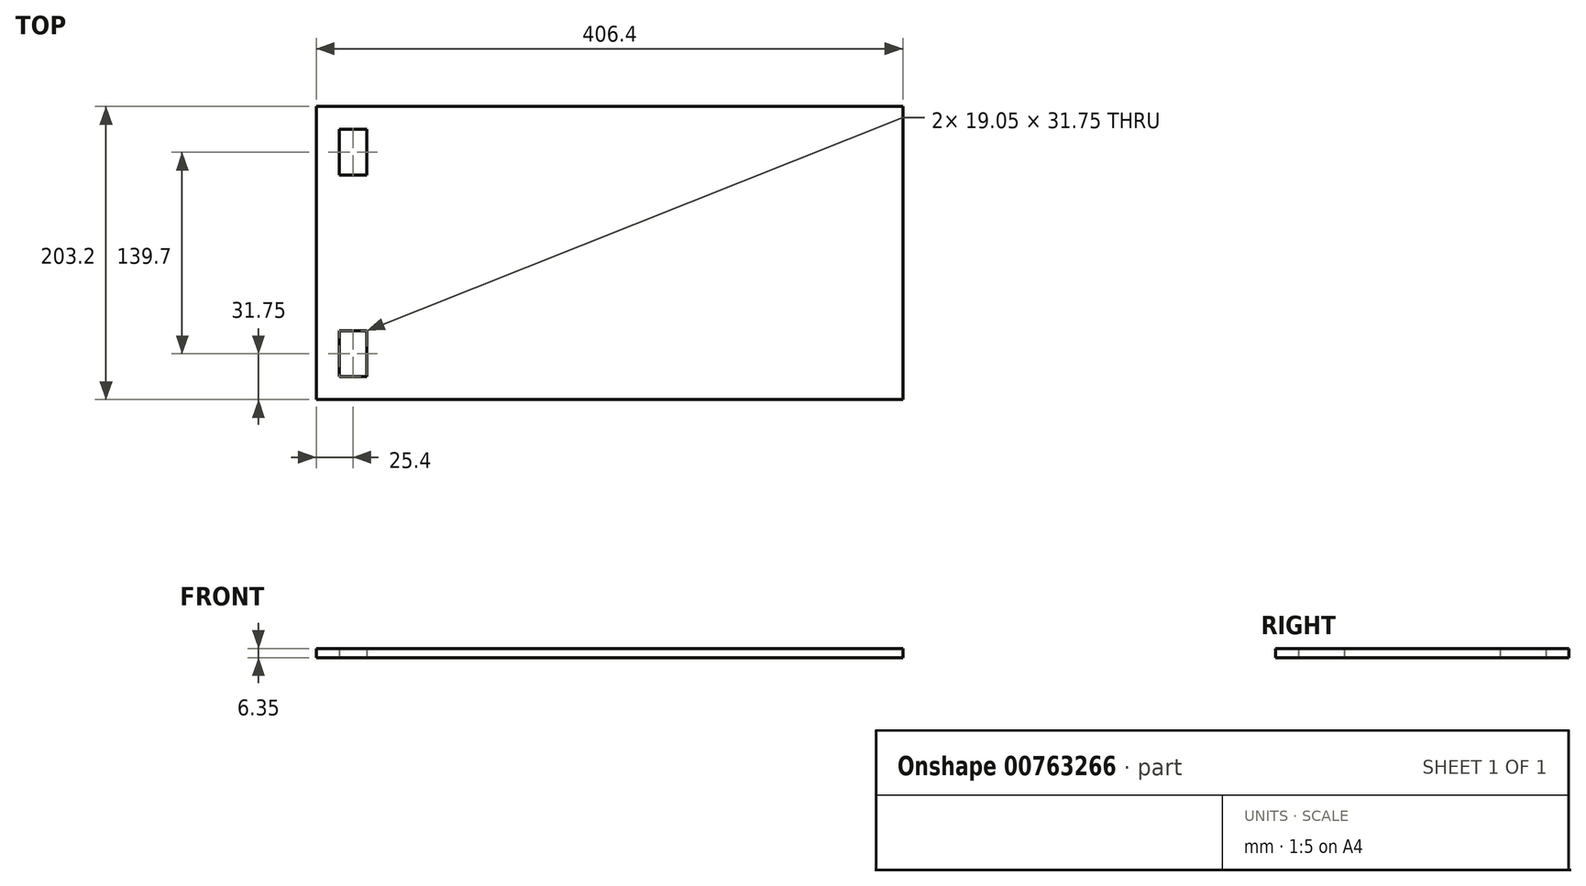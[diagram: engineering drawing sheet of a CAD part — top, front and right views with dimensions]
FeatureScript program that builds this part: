
annotation { "Feature Type Name" : "Feature", "Feature Type Description" : "" }
export const myFeature = defineFeature(function(context is Context, id is Id, definition is map)
    precondition{}
    {
        {
            var Q0;
            Q0=qCreatedBy(makeId("Top.planeOp"),FACE);
            var sketch = newSketch(context, id + "F0", { "sketchPlane" : qUnion([Q0])});
            skLineSegment(sketch, "E0.bottom", {"start": v(203.2, -101.6) * mm, "end": v(-203.2, -101.6) * mm});
            skLineSegment(sketch, "E0.top", {"start": v(203.2, 101.6) * mm, "end": v(-203.2, 101.6) * mm});
            skLineSegment(sketch, "E0.left", {"start": v(203.2, -101.6) * mm, "end": v(203.2, 101.6) * mm});
            skLineSegment(sketch, "E0.right", {"start": v(-203.2, -101.6) * mm, "end": v(-203.2, 101.6) * mm});
            skPoint(sketch, "E0.middle", {"position": v(0, 0) * mm});
            skLineSegment(sketch, "E1.bottom", {"start": v(-168.27, -53.98) * mm, "end": v(-187.32, -53.98) * mm});
            skLineSegment(sketch, "E1.top", {"start": v(-168.27, -85.73) * mm, "end": v(-187.32, -85.73) * mm});
            skLineSegment(sketch, "E1.left", {"start": v(-168.27, -53.98) * mm, "end": v(-168.27, -85.73) * mm});
            skLineSegment(sketch, "E1.right", {"start": v(-187.32, -53.98) * mm, "end": v(-187.32, -85.73) * mm});
            skPoint(sketch, "E1.middle", {"position": v(-177.8, -69.85) * mm});
            skLineSegment(sketch, "E2.bottom", {"start": v(-168.28, 53.97) * mm, "end": v(-187.33, 53.97) * mm});
            skLineSegment(sketch, "E2.top", {"start": v(-168.28, 85.72) * mm, "end": v(-187.33, 85.72) * mm});
            skLineSegment(sketch, "E2.left", {"start": v(-168.28, 53.97) * mm, "end": v(-168.28, 85.72) * mm});
            skLineSegment(sketch, "E2.right", {"start": v(-187.33, 53.97) * mm, "end": v(-187.33, 85.72) * mm});
            skPoint(sketch, "E2.middle", {"position": v(-177.8, 69.85) * mm});
            skPoint(sketch, "E3.endSnap0", {"position": v(-177.82, 0) * mm});
            skLineSegment(sketch, "E4", {"start": v(-177.8, 69.85) * mm, "end": v(-177.8, -69.85) * mm, "construction": true});
            skSolve(sketch);
        }
        {
            var Q0;
            Q0 = qSketchRegion(id + "F0", true);
            extrude(context, id + "F1", {"entities" : qUnion([Q0]), "depth" : 6.35 * mm, "offsetDistance" : 25.4 * mm});
        }
    });
